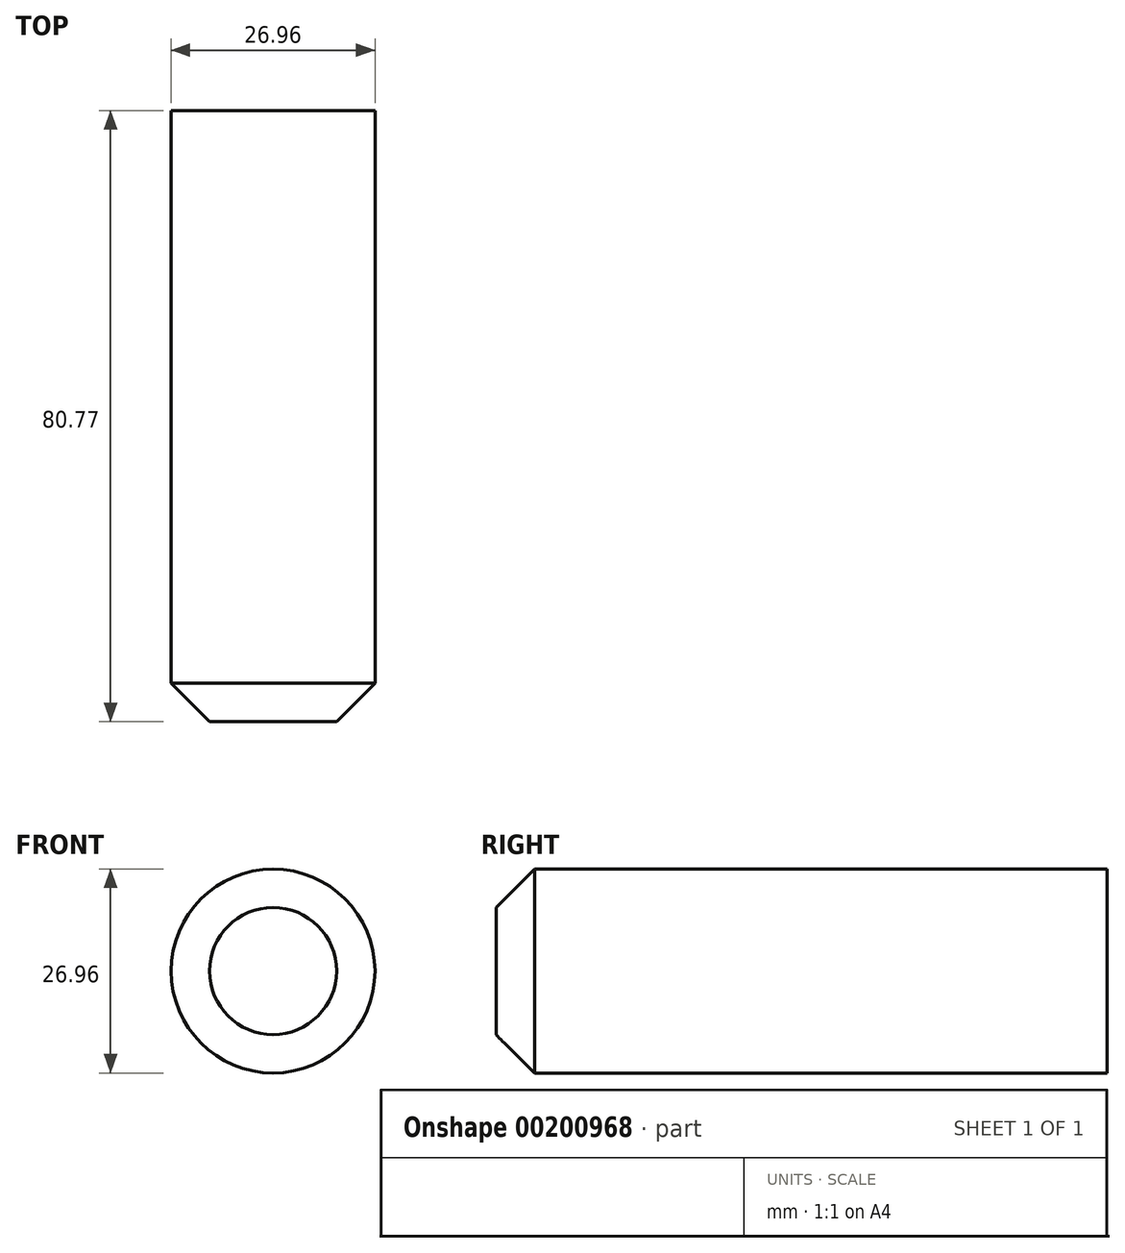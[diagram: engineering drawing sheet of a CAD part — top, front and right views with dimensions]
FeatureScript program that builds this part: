
annotation { "Feature Type Name" : "Feature", "Feature Type Description" : "" }
export const myFeature = defineFeature(function(context is Context, id is Id, definition is map)
    precondition{}
    {
        {
            var Q0;
            Q0=qCreatedBy(makeId("Front.planeOp"),FACE);
            var sketch = newSketch(context, id + "F0", { "sketchPlane" : qUnion([Q0])});
            skCircle(sketch, "E0", {"center": v(-22.9, -2.05) * mm, "radius": 13.48 * mm});
            skSolve(sketch);
        }
        {
            var Q0;
            Q0 = qSketchRegion(id + "F0", true);
            extrude(context, id + "F1", {"entities" : qUnion([Q0]), "oppositeDirection" : true, "depth" : 55.37 * mm});
        }
        {
            var Q0;
            Q0=makeQuery(id+"F1.opExtrude","CAP_EDGE",EDGE,{"disambiguationData":[OSD([sQuery(id+"F0.wireOp",EDGE,"E0")])],"isStart":true});
            var Q1;
            Q1=makeQuery(id+"F1.opExtrude","CAP_FACE",FACE,{"disambiguationData":[OSD([sQuery(id+"F0.wireOp",EDGE,"E0")])],"isStart":true});
            chamfer(context, id + "F2", {"entities" : qUnion([Q0, Q1]), "width" : 5.08 * mm, "tangentPropagation" : true});
        }
        {
            var Q0;
            Q0=makeQuery(id+"F1.opExtrude","CAP_FACE",FACE,{"disambiguationData":[OSD([sQuery(id+"F0.wireOp",EDGE,"E0")])],"isStart":false});
            extrude(context, id + "F3", {"entities" : qUnion([Q0]), "operationType" : NewBodyOperationType.ADD, "depth" : 25.4 * mm});
        }
    });
